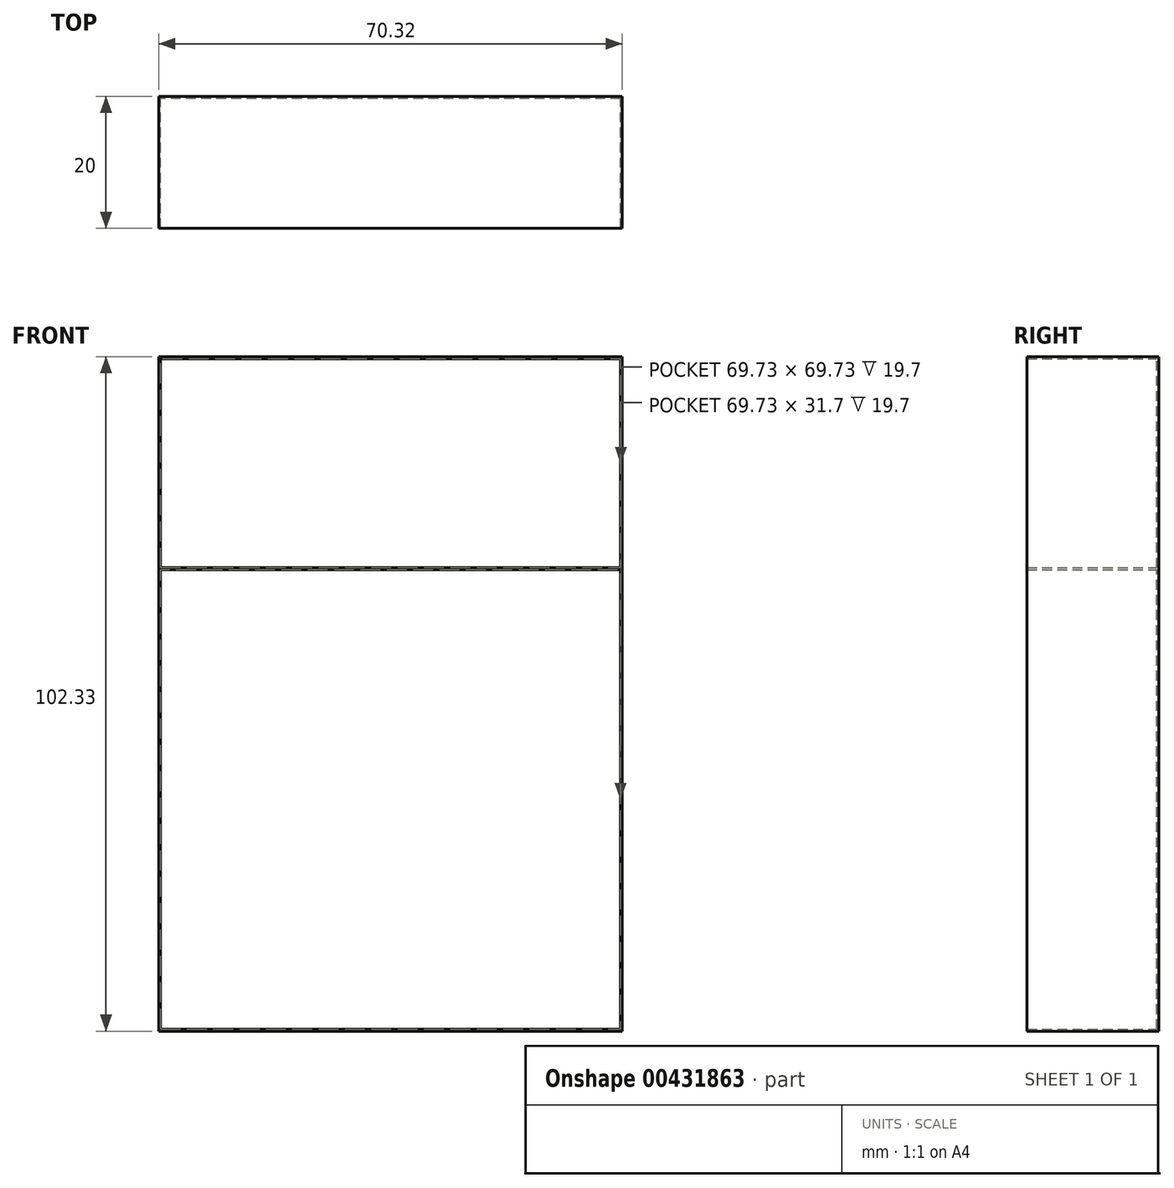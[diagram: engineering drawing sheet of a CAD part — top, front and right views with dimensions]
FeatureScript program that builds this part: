
annotation { "Feature Type Name" : "Feature", "Feature Type Description" : "" }
export const myFeature = defineFeature(function(context is Context, id is Id, definition is map)
    precondition{}
    {
        {
            var Q0;
            Q0=qCreatedBy(makeId("Front.planeOp"),FACE);
            var sketch = newSketch(context, id + "F0", { "sketchPlane" : qUnion([Q0])});
            skLineSegment(sketch, "E0.bottom", {"start": v(35.16, -35.16) * mm, "end": v(-35.16, -35.17) * mm});
            skLineSegment(sketch, "E0.top", {"start": v(35.16, 35.16) * mm, "end": v(-35.16, 35.16) * mm});
            skLineSegment(sketch, "E0.left", {"start": v(35.16, -35.16) * mm, "end": v(35.16, 35.16) * mm});
            skLineSegment(sketch, "E0.right", {"start": v(-35.16, -35.17) * mm, "end": v(-35.16, 35.16) * mm});
            skLineSegment(sketch, "E1", {"start": v(0, 50.16) * mm, "end": v(0, -40.93) * mm, "construction": true});
            skLineSegment(sketch, "E2.bottom", {"start": v(35.16, 35.16) * mm, "end": v(-35.17, 35.16) * mm});
            skLineSegment(sketch, "E2.top", {"start": v(35.16, 67.17) * mm, "end": v(-35.17, 67.17) * mm});
            skLineSegment(sketch, "E2.left", {"start": v(35.16, 35.16) * mm, "end": v(35.16, 67.17) * mm});
            skLineSegment(sketch, "E2.right", {"start": v(-35.17, 35.16) * mm, "end": v(-35.17, 67.17) * mm});
            skSolve(sketch);
        }
        {
            var Q0;
            Q0=makeQuery(id+"F0.imprint","IMPRINT",FACE,{"disambiguationData":[TD([[makeQuery(id+"F0.imprint","IMPRINT",EDGE,{"derivedFrom":sQuery(id+"F0.wireOp",EDGE,"E0.bottom")}),-1.0]])]});
            extrude(context, id + "F1", {"entities" : qUnion([Q0]), "depth" : 20 * mm});
        }
        {
            var Q0;
            Q0=makeQuery(id+"F1.opExtrude","CAP_FACE",FACE,{"disambiguationData":[OSD([sQuery(id+"F0.wireOp",EDGE,"E0.bottom"),sQuery(id+"F0.wireOp",EDGE,"E0.top"),sQuery(id+"F0.wireOp",EDGE,"E0.left"),sQuery(id+"F0.wireOp",EDGE,"E0.right")])],"isStart":false});
            shell(context, id + "F2", {"entities" : qUnion([Q0]), "thickness" : 0.3 * mm});
        }
        {
            var Q0;
            Q0=makeQuery(id+"F0.imprint","IMPRINT",FACE,{"disambiguationData":[TD([[makeQuery(id+"F0.imprint","IMPRINT",EDGE,{"derivedFrom":sQuery(id+"F0.wireOp",EDGE,"E2.bottom")}),-1.0]])]});
            extrude(context, id + "F3", {"entities" : qUnion([Q0]), "operationType" : NewBodyOperationType.ADD, "depth" : 20 * mm});
        }
        {
            var Q0;
            {var subQ0=sQuery(id+"F0.wireOp",EDGE,"E2.bottom");Q0=makeQuery(id+"F3.boolean.opBoolean","MERGE",FACE,{"derivedFrom":[makeQuery(id+"F1.opExtrude","CAP_FACE",FACE,{"disambiguationData":[OSD([sQuery(id+"F0.wireOp",EDGE,"E0.bottom"),sQuery(id+"F0.wireOp",EDGE,"E0.left"),sQuery(id+"F0.wireOp",EDGE,"E0.right"),subQ0])],"isStart":false}),makeQuery(id+"F3.opExtrude","CAP_FACE",FACE,{"disambiguationData":[OSD([subQ0,sQuery(id+"F0.wireOp",EDGE,"E2.top"),sQuery(id+"F0.wireOp",EDGE,"E2.left"),sQuery(id+"F0.wireOp",EDGE,"E2.right")])],"isStart":false})]});}
            shell(context, id + "F4", {"entities" : qUnion([Q0]), "thickness" : 0.3 * mm});
        }
    });
